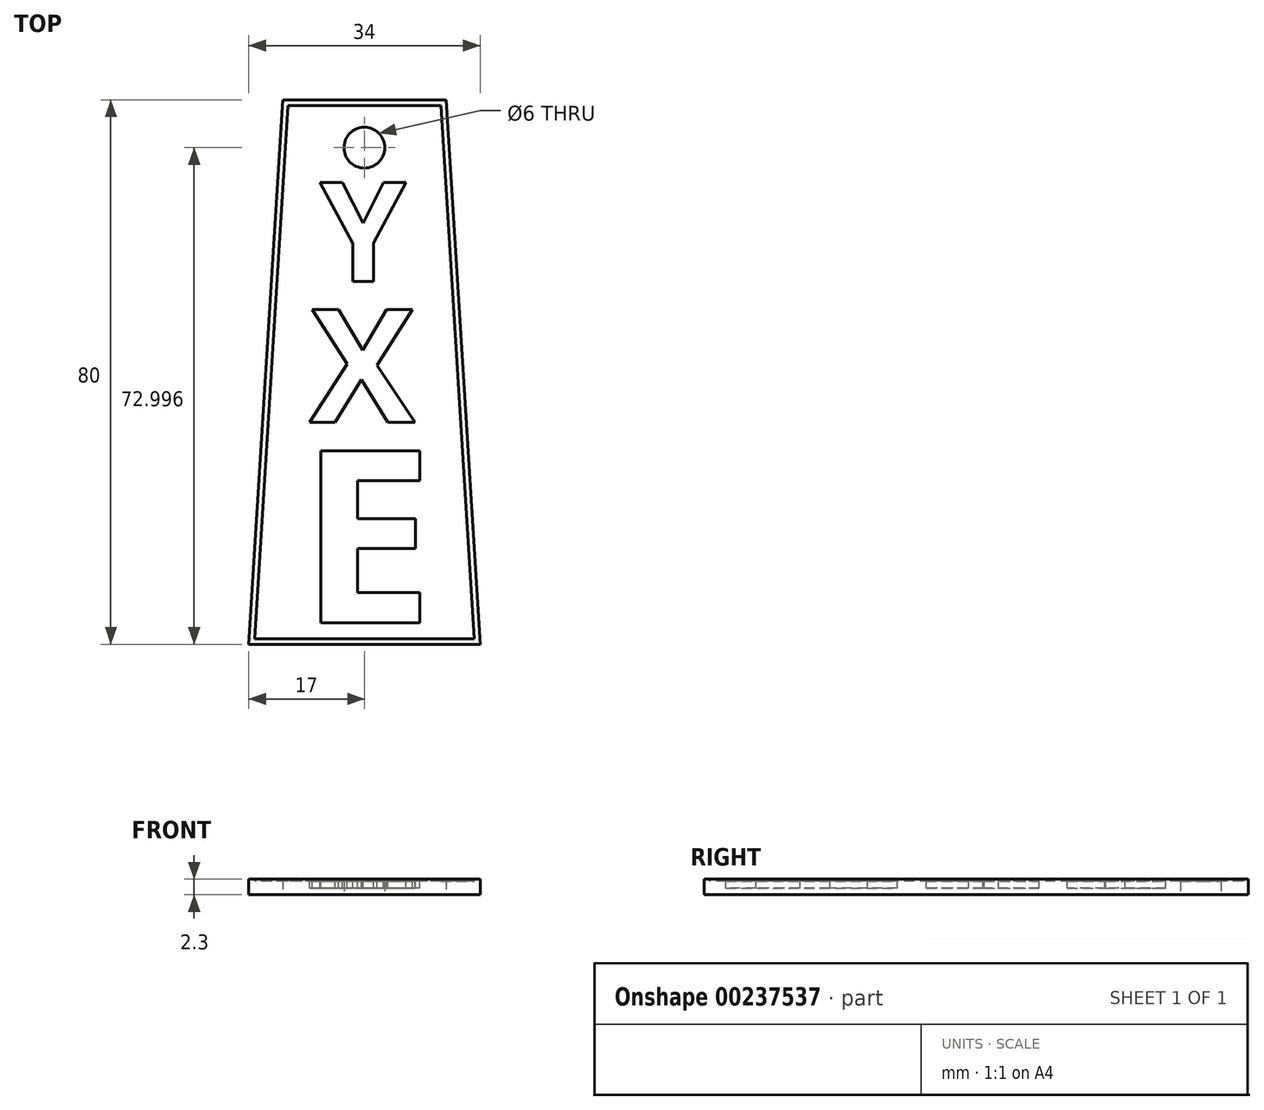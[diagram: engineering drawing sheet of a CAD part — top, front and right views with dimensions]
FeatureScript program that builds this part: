
annotation { "Feature Type Name" : "Feature", "Feature Type Description" : "" }
export const myFeature = defineFeature(function(context is Context, id is Id, definition is map)
    precondition{}
    {
        {
            var Q0;
            Q0=qCreatedBy(makeId("Top.planeOp"),FACE);
            var sketch = newSketch(context, id + "F0", { "sketchPlane" : qUnion([Q0])});
            skLineSegment(sketch, "E0.bottom", {"start": v(0, 44.94) * mm, "end": v(-12, 44.94) * mm});
            skLineSegment(sketch, "E0.top", {"start": v(0, -35.06) * mm, "end": v(-17, -35.06) * mm});
            skLineSegment(sketch, "E0.right", {"start": v(-12, 44.94) * mm, "end": v(-17, -35.06) * mm});
            skPoint(sketch, "E0.middle", {"position": v(0, 0) * mm});
            skLineSegment(sketch, "E1", {"start": v(0, 0) * mm, "end": v(0, 44.94) * mm});
            skLineSegment(sketch, "E2.MirrorCS", {"start": v(0, 44.94) * mm, "end": v(12, 44.94) * mm});
            skLineSegment(sketch, "E3.MirrorCS", {"start": v(12, 44.94) * mm, "end": v(17, -35.06) * mm});
            skLineSegment(sketch, "E4", {"start": v(0, 0) * mm, "end": v(0, -35.06) * mm});
            skPoint(sketch, "E4.endSnap0", {"position": v(0, 22.47) * mm});
            skLineSegment(sketch, "E5.MirrorCS", {"start": v(0, -35.06) * mm, "end": v(17, -35.06) * mm});
            skCircle(sketch, "E6", {"center": v(0, 37.94) * mm, "radius": 3 * mm});
            skSolve(sketch);
        }
        {
            var Q0;
            {var subQ5=sQuery(id+"F0.wireOp",EDGE,"E0.bottom");Q0=makeQuery(id+"F0.imprint","IMPRINT",FACE,{"disambiguationData":[TD([[makeQuery(id+"F0.imprint","IMPRINT",EDGE,{"derivedFrom":subQ5}),1.0]])]});}
            var Q1;
            {var subQ0=sQuery(id+"F0.wireOp",EDGE,"E2.MirrorCS");Q1=makeQuery(id+"F0.imprint","IMPRINT",FACE,{"disambiguationData":[TD([[makeQuery(id+"F0.imprint","IMPRINT",EDGE,{"derivedFrom":subQ0}),-1.0]])]});}
            extrude(context, id + "F1", {"entities" : qUnion([Q0, Q1]), "depth" : 2 * mm});
        }
        {
            var Q0;
            Q0=makeQuery(id+"F1.opExtrude","CAP_FACE",FACE,{"disambiguationData":[OSD([sQuery(id+"F0.wireOp",EDGE,"E0.bottom"),sQuery(id+"F0.wireOp",EDGE,"E0.top"),sQuery(id+"F0.wireOp",EDGE,"E0.right"),sQuery(id+"F0.wireOp",EDGE,"E2.MirrorCS"),sQuery(id+"F0.wireOp",EDGE,"E3.MirrorCS"),sQuery(id+"F0.wireOp",EDGE,"E5.MirrorCS"),sQuery(id+"F0.wireOp",EDGE,"E6")])],"isStart":false});
            var sketch = newSketch(context, id + "F2", { "sketchPlane" : qUnion([Q0])});
            skText(sketch, "E7", { "text": "Y", "fontName": "OpenSans-Bold.ttf"});
            skText(sketch, "E8", { "text": "X", "fontName": "OpenSans-Bold.ttf"});
            skText(sketch, "E9", { "text": "E", "fontName": "OpenSans-Bold.ttf"});
            const initialGuessF2  = {"E7": [-0.00655, 0.0183, 1, 0, 0.01463], "E8": [-0.00805, -0.00242, 1, 0, 0.01672], "E9": [-0.00955, -0.03187, 1, 0, 0.02545]};
            skSetInitialGuess(sketch, initialGuessF2);
            skSolve(sketch);
        }
        {
            var Q0;
            Q0=makeQuery(id+"F2.imprint","IMPRINT",FACE,{"disambiguationData":[TD([[makeQuery(id+"F2.imprint","IMPRINT",EDGE,{"derivedFrom":sQuery(id+"F2.wireOp",EDGE,"E9.sketch_text.stroke-0")}),-1.0]])]});
            var Q1;
            Q1=makeQuery(id+"F2.imprint","IMPRINT",FACE,{"disambiguationData":[TD([[makeQuery(id+"F2.imprint","IMPRINT",EDGE,{"derivedFrom":sQuery(id+"F2.wireOp",EDGE,"E8.sketch_text.stroke-0")}),-1.0]])]});
            var Q2;
            Q2=makeQuery(id+"F2.imprint","IMPRINT",FACE,{"disambiguationData":[TD([[makeQuery(id+"F2.imprint","IMPRINT",EDGE,{"derivedFrom":sQuery(id+"F2.wireOp",EDGE,"E7.sketch_text.stroke-0")}),-1.0]])]});
            extrude(context, id + "F3", {"entities" : qUnion([Q0, Q1, Q2]), "operationType" : NewBodyOperationType.REMOVE, "oppositeDirection" : true, "depth" : 1 * mm});
        }
        {
            var Q0;
            Q0=makeQuery(id+"F1.opExtrude","CAP_FACE",FACE,{"disambiguationData":[OSD([sQuery(id+"F0.wireOp",EDGE,"E0.bottom"),sQuery(id+"F0.wireOp",EDGE,"E0.top"),sQuery(id+"F0.wireOp",EDGE,"E0.right"),sQuery(id+"F0.wireOp",EDGE,"E2.MirrorCS"),sQuery(id+"F0.wireOp",EDGE,"E3.MirrorCS"),sQuery(id+"F0.wireOp",EDGE,"E5.MirrorCS"),sQuery(id+"F0.wireOp",EDGE,"E6")])],"isStart":false});
            var sketch = newSketch(context, id + "F4", { "sketchPlane" : qUnion([Q0])});
            skLineSegment(sketch, "E10.0", {"start": v(-12, 44.94) * mm, "end": v(-17, -35.06) * mm});
            skLineSegment(sketch, "E11.0", {"start": v(12, 44.94) * mm, "end": v(-12, 44.94) * mm});
            skLineSegment(sketch, "E12.0", {"start": v(12, 44.94) * mm, "end": v(17, -35.06) * mm});
            skLineSegment(sketch, "E13.0", {"start": v(17, -35.06) * mm, "end": v(-17, -35.06) * mm});
            skLineSegment(sketch, "E14.0", {"start": v(11.25, 44.14) * mm, "end": v(16.15, -34.26) * mm});
            skLineSegment(sketch, "E14.1", {"start": v(11.25, 44.14) * mm, "end": v(-11.25, 44.14) * mm});
            skLineSegment(sketch, "E14.2", {"start": v(-11.25, 44.14) * mm, "end": v(-16.15, -34.26) * mm});
            skLineSegment(sketch, "E14.3", {"start": v(16.15, -34.26) * mm, "end": v(-16.15, -34.26) * mm});
            skSolve(sketch);
        }
        {
            var Q0;
            Q0 = qSketchRegion(id + "F4", true);
            extrude(context, id + "F5", {"entities" : qUnion([Q0]), "operationType" : NewBodyOperationType.ADD, "depth" : .3 * mm});
        }
    });
